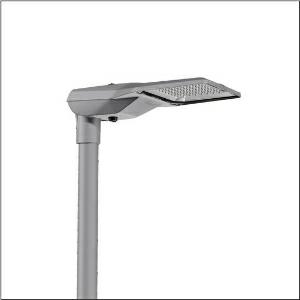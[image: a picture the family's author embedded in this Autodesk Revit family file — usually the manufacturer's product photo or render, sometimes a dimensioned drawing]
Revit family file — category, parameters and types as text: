
# Revit family: streetlight_sl_21_midi___stw1_0a_5xe3e23t08nb_45a6
name_source: partatom
category: Lighting Fixtures
units: mm (PartAtom-declared; Revit-internal decimal feet)

## family parameters
Cut with Voids When Loaded = No
Host = Face
Light Source = No
Part Type = Normal
Room Calculation Point = No
Round Connector Dimension = Use Diameter
Shared = No

## types (1)
- --- (1 x LED, 18780 lm, 151.2 W, 2200K)
    Apparent Load = 151 VA
    CIE Flux Codes = 39 75 98 100 100
    Color Rendering = 70
    Color Temperature = 2200K
    Default Elevation = 1800 mm
    Description = Streetlight SL 21 midi, mast luminaire, primary light control with lens, of PMMA, primary optical cover: cover, of toughened safety glass, transparent, light distribution: STW1.0a, light emission: direct distribution, primary light characteristic: asymmetric, installation type: side-entry, post-top, LED, High Power LED, rated luminous flux: 18.780lm, luminous efficacy: 124lm/W, light colour: 722, colour temperature: 2200K, control gear: D4i, control: overheat protection, constant luminous flux control, time-dependent luminous flux control, flexible luminous flux parameterisation, pre-setting: logarithmic dimming characteristic, mains connection: 230..240V, AC, 50/60Hz, start of lifetime: 151W, end of service life: 157W, reduction: 70W, luminaire housing, of diecast aluminium, powder-coated, Siteco® metallic grey (DB 702S), corrosivity category C5 mid according to DIN EN ISO 12944, please order mast flange separately, inclination adjustable: 0°, 5°, 10°, 15°, sealing non-destructively replaceable, multi-level sealing system, length: 644mm, width: 335mm, height: 110mm, mast flange for spigot size: 42mm (side-entry): 5XC10008XM4, 60/48mm (side-entry/post-top): 5XC10108XM2, 76/60mm (side-entry/post-top): 5XC10108XM1, mounting height: 4..8m, Smart Interface below and above, protection rating (complete): IP66, insulation class (complete): insulation class II (safety insulation), certification: CE, ENEC, ENEC+, VDE, impact resistance: IK10, permissible operating ambient temperature for outdoor applications: -40..+50°C, standard-compliant lighting for roads and squares, packaging unit: 1 piece

Light Distribution: STW1.0a
    Height = 111 mm
    Lamp = 1 x LED
    Lamp Light Flux = 18780 lm
    Lamp Power = 151.2 W
    Lamp count = 1
    Length = 644 mm
    Luminous efficacy = 124 lm/W
    Manufacturer = Siteco
    ModVariant = No
    Model = 5XE3E23T08NB
    Number of Poles = 1
    OnlyDefault = Yes
    Power Factor = 1
    Product Name = Streetlight SL 21 midi | STW1.0a
    Product group = mast luminaire | pylon top
    ProductGroupID = 6100
    Protection Class = Protection class II
    Protection Degree = IP 66
    RLX_Detail_Level = 1
    RLX_Emergency_Light_Flux = 0 lm
    RLX_Emergency_Type = 0
    RLX_Emergency_Type_DB = No
    RlxData = <blob elided: 27153 chars, md5=606238bd>
    Socket = socket
    Standby Power = 0 W
    System Light Flux = 18781 lm
    System Power = 151 W
    Type Comments = factory setting: luminous flux: 100 % | dim-lin: 254 | 802 mA
    Type Image = l_1004304.jpg
    URL = http://relux.com
    VarID = @adj_169610
    Voltage = 0 V
    Weight = 0.00 kg
    Width = 336 mm

## geometry (parser evidence)
native form markers: Blend x4, Sweep x12
no freeform markers — native parametric forms only
